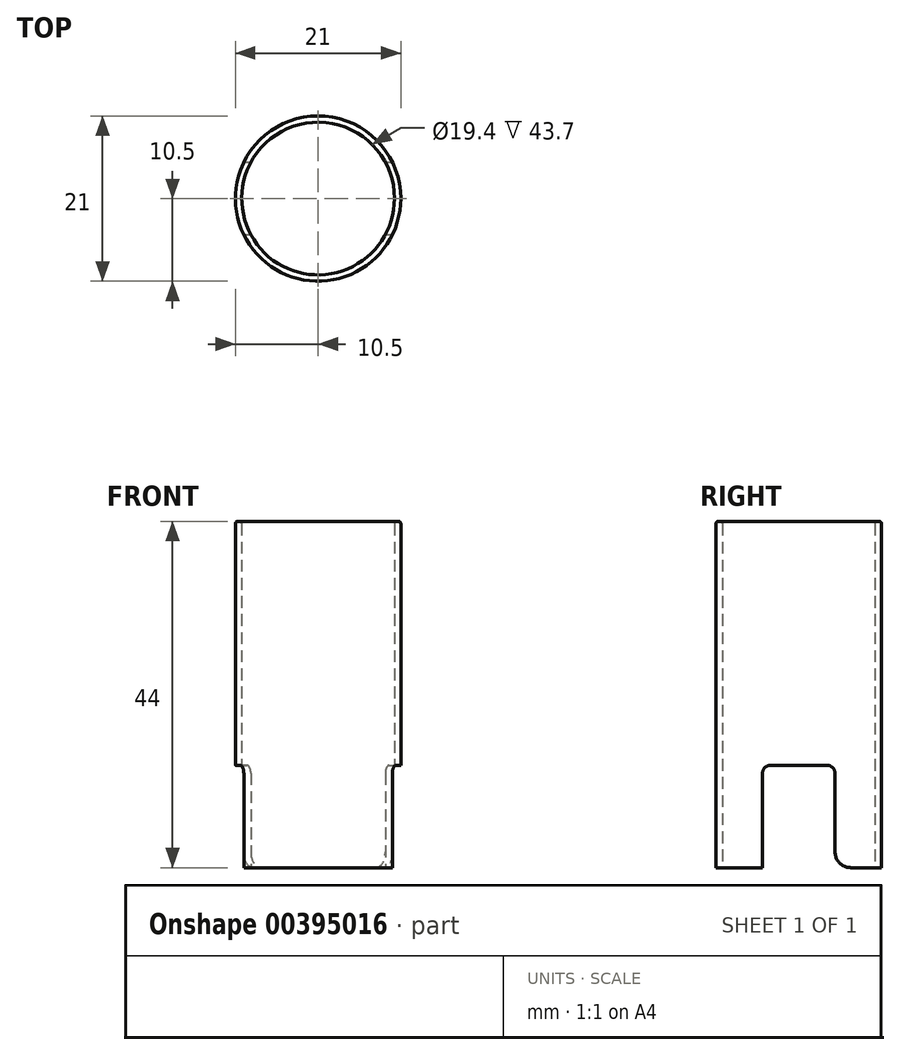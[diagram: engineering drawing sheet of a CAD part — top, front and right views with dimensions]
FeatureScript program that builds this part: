
annotation { "Feature Type Name" : "Feature", "Feature Type Description" : "" }
export const myFeature = defineFeature(function(context is Context, id is Id, definition is map)
    precondition{}
    {
        {
            var Q0;
            Q0=qCreatedBy(makeId("Top.planeOp"),FACE);
            var sketch = newSketch(context, id + "F0", { "sketchPlane" : qUnion([Q0])});
            skCircle(sketch, "E0", {"center": v(0, 0) * mm, "radius": 9.7 * mm});
            skCircle(sketch, "E1", {"center": v(0, 0) * mm, "radius": 10.5 * mm});
            skSolve(sketch);
        }
        {
            var Q0;
            Q0=qSketchRegion(id+"F0",true);
            extrude(context, id + "F1", {"entities" : qUnion([Q0]), "depth" : 44 * mm});
        }
        {
            var Q0;
            Q0=qCreatedBy(makeId("Right.planeOp"),FACE);
            var sketch = newSketch(context, id + "F2", { "sketchPlane" : qUnion([Q0])});
            skLineSegment(sketch, "E2", {"start": v(-11.3, -7.5) * mm, "end": v(-11.3, 0) * mm});
            skLineSegment(sketch, "E3", {"start": v(-11.3, 0) * mm, "end": v(-4.6, 0) * mm});
            skLineSegment(sketch, "E4", {"start": v(-4.6, 0) * mm, "end": v(-4.6, 13) * mm});
            skLineSegment(sketch, "E5", {"start": v(-4.6, 13) * mm, "end": v(4.6, 13) * mm});
            skLineSegment(sketch, "E6", {"start": v(4.6, 13) * mm, "end": v(4.6, 0) * mm});
            skLineSegment(sketch, "E7", {"start": v(4.6, 0) * mm, "end": v(11.3, 0) * mm});
            skLineSegment(sketch, "E8", {"start": v(11.3, 0) * mm, "end": v(11.3, -7.5) * mm});
            skLineSegment(sketch, "E9", {"start": v(11.3, -7.5) * mm, "end": v(-11.3, -7.5) * mm});
            skSolve(sketch);
        }
        {
            var Q0;
            Q0=makeQuery(id+"F2.imprint","IMPRINT",FACE,{"disambiguationData":[TD([[makeQuery(id+"F2.imprint","IMPRINT",EDGE,{"derivedFrom":sQuery(id+"F2.wireOp",EDGE,"E2")}),-1.0]])]});
            extrude(context, id + "F3", {"entities" : qUnion([Q0]), "operationType" : NewBodyOperationType.REMOVE, "endBound" : BoundingType.SYMMETRIC, "oppositeDirection" : true, "depth" : 41.5 * mm});
        }
        {
            var Q0;
            Q0=makeQuery(id+"F3.boolean.opBoolean","COPY",EDGE,{"disambiguationData":[OD(1.0)],"derivedFrom":makeQuery(id+"F3.opExtrude","SWEPT_EDGE",EDGE,{"disambiguationData":[OSD([sQuery(id+"F2.wireOp",EDGE,"E3"),sQuery(id+"F2.wireOp",EDGE,"E4")])]})});
            var Q1;
            Q1=makeQuery(id+"F3.boolean.opBoolean","COPY",EDGE,{"disambiguationData":[OD(0.0)],"derivedFrom":makeQuery(id+"F3.opExtrude","SWEPT_EDGE",EDGE,{"disambiguationData":[OSD([sQuery(id+"F2.wireOp",EDGE,"E6"),sQuery(id+"F2.wireOp",EDGE,"E7")])]})});
            var Q2;
            Q2=makeQuery(id+"F3.boolean.opBoolean","COPY",EDGE,{"disambiguationData":[OD(1.0)],"derivedFrom":makeQuery(id+"F3.opExtrude","SWEPT_EDGE",EDGE,{"disambiguationData":[OSD([sQuery(id+"F2.wireOp",EDGE,"E6"),sQuery(id+"F2.wireOp",EDGE,"E7")])]})});
            var Q3;
            Q3=makeQuery(id+"F3.boolean.opBoolean","COPY",EDGE,{"disambiguationData":[OD(0.0)],"derivedFrom":makeQuery(id+"F3.opExtrude","SWEPT_EDGE",EDGE,{"disambiguationData":[OSD([sQuery(id+"F2.wireOp",EDGE,"E3"),sQuery(id+"F2.wireOp",EDGE,"E4")])]})});
            fillet(context, id + "F4", {"entities" : qUnion([Q0, Q1, Q2, Q3]), "radius" : 2 * mm, "tangentPropagation" : true, "allowEdgeOverflow" : false});
        }
        {
            var Q0;
            Q0=makeQuery(id+"F1.opExtrude","CAP_EDGE",EDGE,{"disambiguationData":[OSD([sQuery(id+"F0.wireOp",EDGE,"E1")])],"isStart":false});
            var Q1;
            Q1=makeQuery(id+"F1.opExtrude","CAP_EDGE",EDGE,{"disambiguationData":[OSD([sQuery(id+"F0.wireOp",EDGE,"E0")])],"isStart":false});
            fillet(context, id + "F5", {"entities" : qUnion([Q0, Q1]), "radius" : .3 * mm, "tangentPropagation" : true, "allowEdgeOverflow" : false});
        }
        {
            var Q0;
            Q0=makeQuery(id+"F3.boolean.opBoolean","COPY",EDGE,{"disambiguationData":[OD(1.0)],"derivedFrom":makeQuery(id+"F3.opExtrude","SWEPT_EDGE",EDGE,{"disambiguationData":[OSD([sQuery(id+"F2.wireOp",EDGE,"E4"),sQuery(id+"F2.wireOp",EDGE,"E5")])]})});
            var Q1;
            Q1=makeQuery(id+"F3.boolean.opBoolean","COPY",EDGE,{"disambiguationData":[OD(1.0)],"derivedFrom":makeQuery(id+"F3.opExtrude","SWEPT_EDGE",EDGE,{"disambiguationData":[OSD([sQuery(id+"F2.wireOp",EDGE,"E5"),sQuery(id+"F2.wireOp",EDGE,"E6")])]})});
            var Q2;
            Q2=makeQuery(id+"F3.boolean.opBoolean","COPY",EDGE,{"disambiguationData":[OD(0.0)],"derivedFrom":makeQuery(id+"F3.opExtrude","SWEPT_EDGE",EDGE,{"disambiguationData":[OSD([sQuery(id+"F2.wireOp",EDGE,"E4"),sQuery(id+"F2.wireOp",EDGE,"E5")])]})});
            var Q3;
            Q3=makeQuery(id+"F3.boolean.opBoolean","COPY",EDGE,{"disambiguationData":[OD(0.0)],"derivedFrom":makeQuery(id+"F3.opExtrude","SWEPT_EDGE",EDGE,{"disambiguationData":[OSD([sQuery(id+"F2.wireOp",EDGE,"E5"),sQuery(id+"F2.wireOp",EDGE,"E6")])]})});
            fillet(context, id + "F6", {"entities" : qUnion([Q0, Q1, Q2, Q3]), "radius" : 1 * mm, "tangentPropagation" : true, "allowEdgeOverflow" : false});
        }
    });
